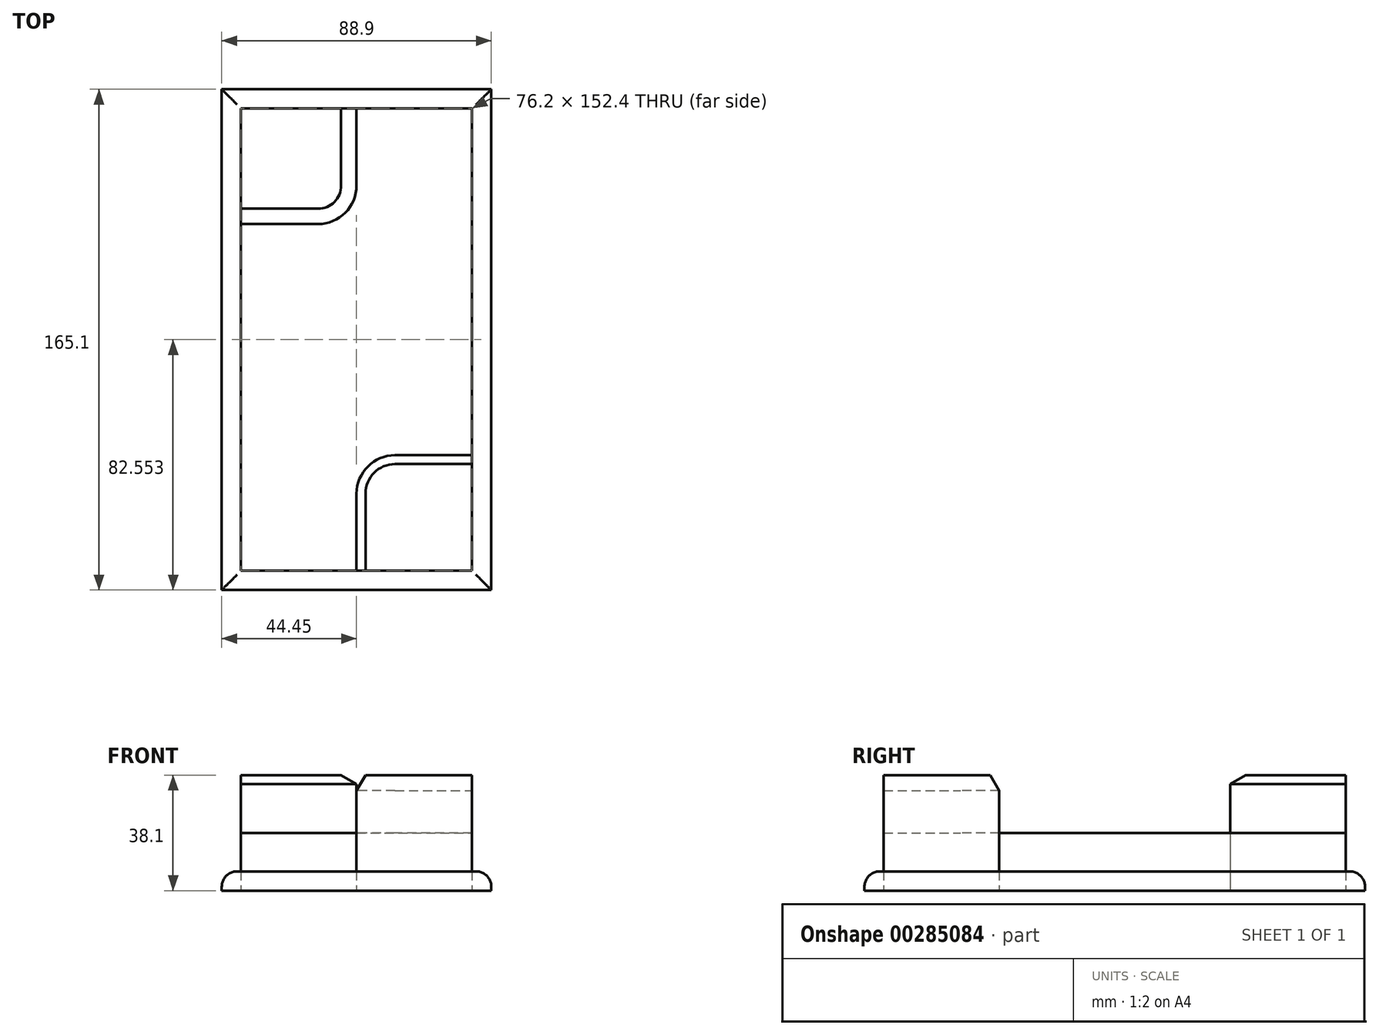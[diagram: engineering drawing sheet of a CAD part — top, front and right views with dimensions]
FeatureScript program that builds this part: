
annotation { "Feature Type Name" : "Feature", "Feature Type Description" : "" }
export const myFeature = defineFeature(function(context is Context, id is Id, definition is map)
    precondition{}
    {
        {
            var Q0;
            Q0=qCreatedBy(makeId("Top.planeOp"),FACE);
            var sketch = newSketch(context, id + "F0", { "sketchPlane" : qUnion([Q0])});
            skLineSegment(sketch, "E0.bottom", {"start": v(-44.45, 77.5) * mm, "end": v(44.45, 77.5) * mm});
            skLineSegment(sketch, "E0.top", {"start": v(-44.45, -87.6) * mm, "end": v(44.45, -87.6) * mm});
            skLineSegment(sketch, "E0.left", {"start": v(-44.45, 77.5) * mm, "end": v(-44.45, -87.6) * mm});
            skLineSegment(sketch, "E0.right", {"start": v(44.45, 77.5) * mm, "end": v(44.45, -87.6) * mm});
            skPoint(sketch, "E1.bottom.start.orphan", {"position": v(-48.4, 77.56) * mm});
            skLineSegment(sketch, "E2.0", {"start": v(38.1, 71.15) * mm, "end": v(38.1, -81.25) * mm});
            skLineSegment(sketch, "E2.1", {"start": v(-38.1, 71.15) * mm, "end": v(38.1, 71.15) * mm});
            skLineSegment(sketch, "E2.2", {"start": v(-38.1, 71.15) * mm, "end": v(-38.1, -81.25) * mm});
            skLineSegment(sketch, "E2.3", {"start": v(-38.1, -81.25) * mm, "end": v(38.1, -81.25) * mm});
            skLineSegment(sketch, "E3", {"start": v(-38.1, 33.05) * mm, "end": v(-12.7, 33.05) * mm});
            skLineSegment(sketch, "E4", {"start": v(38.1, -43.15) * mm, "end": v(12.7, -43.15) * mm});
            skPoint(sketch, "E5.start.orphan", {"position": v(0, 71.15) * mm});
            skLineSegment(sketch, "E6", {"start": v(0, 71.15) * mm, "end": v(0, 45.75) * mm});
            skPoint(sketch, "E7.end.orphan", {"position": v(0, -64.17) * mm});
            skLineSegment(sketch, "E8", {"start": v(0, -81.25) * mm, "end": v(0, -55.85) * mm});
            skPoint(sketch, "E9.newPointB", {"position": v(0, -43.15) * mm});
            skArc(sketch, "E9.filletArc", {"start": v(12.7, -43.15) * mm, "mid": v(3.72, -46.87) * mm, "end": v(0, -55.85) * mm});
            skPoint(sketch, "E10.visualSharp", {"position": v(0, 33.05) * mm});
            skArc(sketch, "E10.filletArc", {"start": v(-12.7, 33.05) * mm, "mid": v(-3.72, 36.77) * mm, "end": v(0, 45.75) * mm});
            skSolve(sketch);
        }
        {
            var Q0;
            {var subQ1=sQuery(id+"F0.wireOp",EDGE,"E3");Q0=makeQuery(id+"F0.imprint","IMPRINT",FACE,{"disambiguationData":[TD([[makeQuery(id+"F0.imprint","IMPRINT",EDGE,{"derivedFrom":subQ1}),1.0]])]});}
            var Q1;
            {var subQ0=sQuery(id+"F0.wireOp",EDGE,"E4");Q1=makeQuery(id+"F0.imprint","IMPRINT",FACE,{"disambiguationData":[TD([[makeQuery(id+"F0.imprint","IMPRINT",EDGE,{"derivedFrom":subQ0}),1.0]])]});}
            extrude(context, id + "F1", {"entities" : qUnion([Q0, Q1]), "depth" : 38.1 * mm});
        }
        {
            var Q0;
            {var subQ8=sQuery(id+"F0.wireOp",EDGE,"E3");Q0=makeQuery(id+"F0.imprint","IMPRINT",FACE,{"disambiguationData":[TD([[makeQuery(id+"F0.imprint","IMPRINT",EDGE,{"derivedFrom":subQ8}),-1.0]])]});}
            extrude(context, id + "F2", {"entities" : qUnion([Q0]), "depth" : 19.05 * mm});
        }
        {
            var Q0;
            Q0=makeQuery(id+"F0.imprint","IMPRINT",FACE,{"disambiguationData":[TD([[makeQuery(id+"F0.imprint","IMPRINT",EDGE,{"derivedFrom":sQuery(id+"F0.wireOp",EDGE,"E0.bottom")}),-1.0]])]});
            extrude(context, id + "F3", {"entities" : qUnion([Q0]), "depth" : 6.35 * mm});
        }
        {
            var Q0;
            Q0=makeQuery(id+"F1.opExtrude","CAP_EDGE",EDGE,{"disambiguationData":[OSD([sQuery(id+"F0.wireOp",EDGE,"E8")])],"isStart":false});
            chamfer(context, id + "F4", {"entities" : qUnion([Q0]), "chamferType" : ChamferType.OFFSET_ANGLE, "width" : 5.08 * mm, "oppositeDirection" : false, "angle" : 30 * degree, "tangentPropagation" : true});
        }
        {
            var Q0;
            Q0=makeQuery(id+"F1.opExtrude","CAP_EDGE",EDGE,{"disambiguationData":[OSD([sQuery(id+"F0.wireOp",EDGE,"E3")])],"isStart":false});
            chamfer(context, id + "F5", {"entities" : qUnion([Q0]), "chamferType" : ChamferType.OFFSET_ANGLE, "width" : 5.08 * mm, "oppositeDirection" : false, "angle" : 30 * degree, "tangentPropagation" : true});
        }
        {
            var Q0;
            Q0=makeQuery(id+"F3.opExtrude","CAP_EDGE",EDGE,{"disambiguationData":[OSD([sQuery(id+"F0.wireOp",EDGE,"E0.top")])],"isStart":false});
            var Q1;
            Q1=makeQuery(id+"F3.opExtrude","CAP_EDGE",EDGE,{"disambiguationData":[OSD([sQuery(id+"F0.wireOp",EDGE,"E0.left")])],"isStart":false});
            var Q2;
            Q2=makeQuery(id+"F3.opExtrude","CAP_EDGE",EDGE,{"disambiguationData":[OSD([sQuery(id+"F0.wireOp",EDGE,"E0.right")])],"isStart":false});
            var Q3;
            Q3=makeQuery(id+"F3.opExtrude","CAP_EDGE",EDGE,{"disambiguationData":[OSD([sQuery(id+"F0.wireOp",EDGE,"E0.bottom")])],"isStart":false});
            fillet(context, id + "F6", {"entities" : qUnion([Q0, Q1, Q2, Q3]), "radius" : 5.08 * mm, "tangentPropagation" : true, "allowEdgeOverflow" : false});
        }
    });
